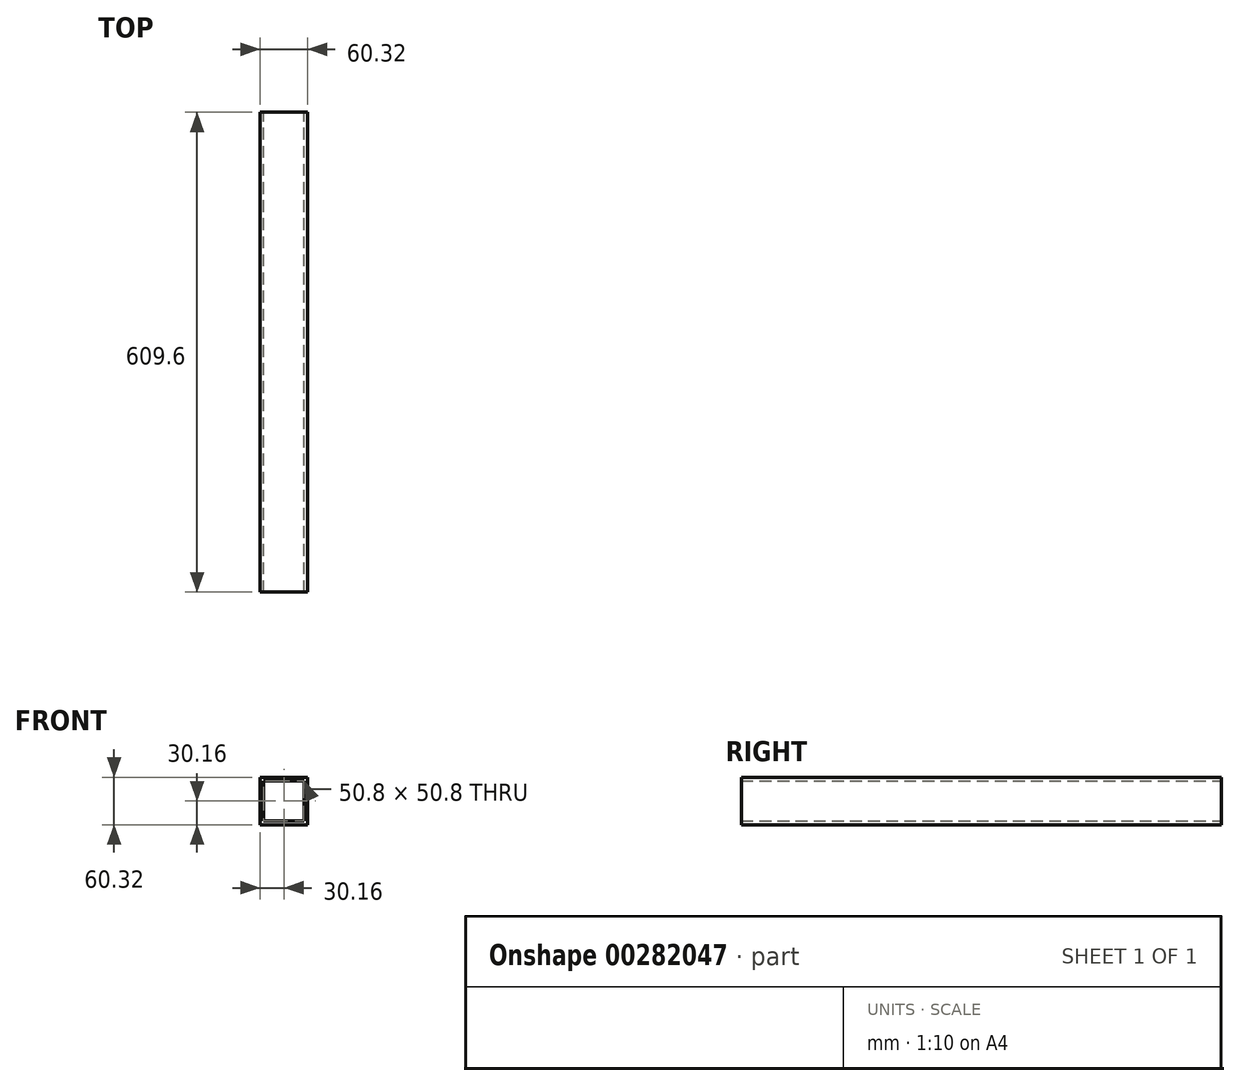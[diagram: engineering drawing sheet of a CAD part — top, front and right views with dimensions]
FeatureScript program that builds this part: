
annotation { "Feature Type Name" : "Feature", "Feature Type Description" : "" }
export const myFeature = defineFeature(function(context is Context, id is Id, definition is map)
    precondition{}
    {
        {
            var Q0;
            Q0=qCreatedBy(makeId("Front.planeOp"),FACE);
            var sketch = newSketch(context, id + "F0", { "sketchPlane" : qUnion([Q0])});
            skLineSegment(sketch, "E0.bottom", {"start": v(30.16, 30.16) * mm, "end": v(-30.16, 30.16) * mm});
            skLineSegment(sketch, "E0.top", {"start": v(30.16, -30.16) * mm, "end": v(-30.16, -30.16) * mm});
            skLineSegment(sketch, "E0.left", {"start": v(30.16, 30.16) * mm, "end": v(30.16, -30.16) * mm});
            skLineSegment(sketch, "E0.right", {"start": v(-30.16, 30.16) * mm, "end": v(-30.16, -30.16) * mm});
            skPoint(sketch, "E0.middle", {"position": v(0, 0) * mm});
            skLineSegment(sketch, "E1.bottom", {"start": v(25.4, 25.4) * mm, "end": v(-25.4, 25.4) * mm});
            skLineSegment(sketch, "E1.top", {"start": v(25.4, -25.4) * mm, "end": v(-25.4, -25.4) * mm});
            skLineSegment(sketch, "E1.left", {"start": v(25.4, 25.4) * mm, "end": v(25.4, -25.4) * mm});
            skLineSegment(sketch, "E1.right", {"start": v(-25.4, 25.4) * mm, "end": v(-25.4, -25.4) * mm});
            skSolve(sketch);
        }
        {
            var Q0;
            Q0 = qSketchRegion(id + "F0", true);
            extrude(context, id + "F1", {"entities" : qUnion([Q0]), "depth" : 609.6 * mm});
        }
    });
